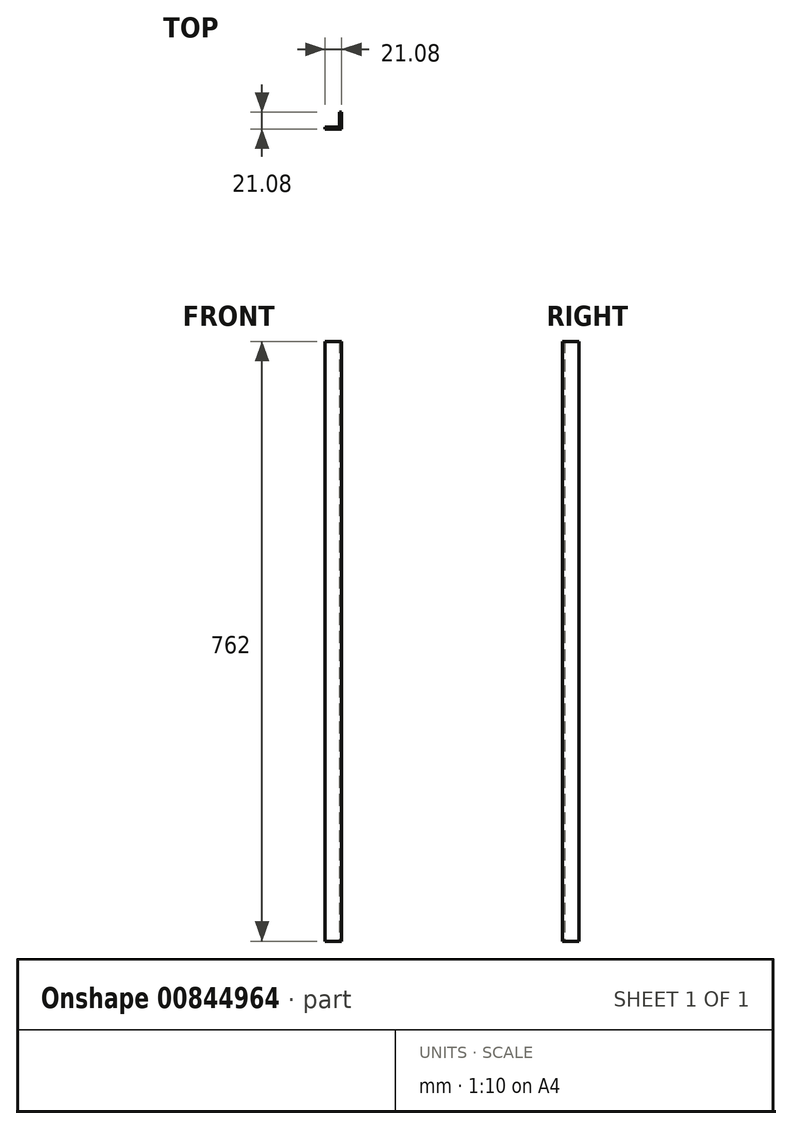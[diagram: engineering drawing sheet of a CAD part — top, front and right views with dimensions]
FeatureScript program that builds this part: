
annotation { "Feature Type Name" : "Feature", "Feature Type Description" : "" }
export const myFeature = defineFeature(function(context is Context, id is Id, definition is map)
    precondition{}
    {
        {
            var Q0;
            Q0=qCreatedBy(makeId("Top.planeOp"),FACE);
            var sketch = newSketch(context, id + "F0", { "sketchPlane" : qUnion([Q0])});
            skLineSegment(sketch, "E0.bottom", {"start": v(0, 0) * mm, "end": v(21.08, 0) * mm});
            skLineSegment(sketch, "E0.left", {"start": v(0, 0) * mm, "end": v(0, 2.54) * mm});
            skLineSegment(sketch, "E0.right", {"start": v(21.08, 0) * mm, "end": v(21.08, 2.9) * mm});
            skLineSegment(sketch, "E1.top", {"start": v(21.08, 21.08) * mm, "end": v(18.54, 21.08) * mm});
            skLineSegment(sketch, "E1.left", {"start": v(21.08, 2.9) * mm, "end": v(21.08, 21.08) * mm});
            skLineSegment(sketch, "E1.right", {"start": v(18.54, 2.54) * mm, "end": v(18.54, 21.08) * mm});
            skLineSegment(sketch, "E2", {"start": v(0, 2.54) * mm, "end": v(18.54, 2.54) * mm});
            skSolve(sketch);
        }
        {
            var Q0;
            Q0 = qSketchRegion(id + "F0", true);
            extrude(context, id + "F1", {"entities" : qUnion([Q0]), "depth" : 762 * mm, "offsetDistance" : 25.4 * mm});
        }
    });
